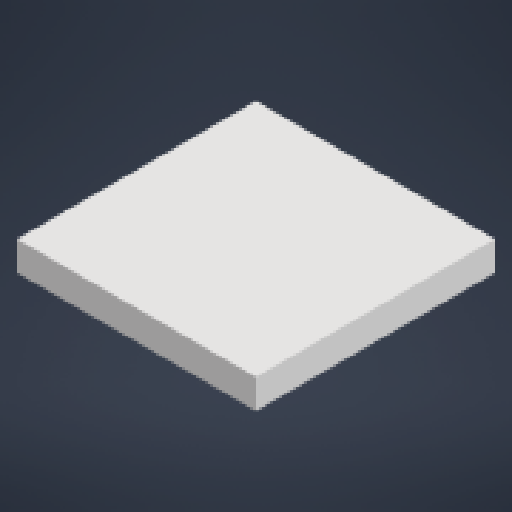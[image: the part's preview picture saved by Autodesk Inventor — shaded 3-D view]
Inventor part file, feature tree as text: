
AUTODESK INVENTOR PART (.ipt)
format: ipt  version: 2023 (Build 270158000, 158)  size: 110,080 bytes
history: native  units: in
note: dims shown in document units (in); Inventor stores cm internally (conversion verified against a paired STEP export)
features: extrude x1, sketch x1
ambient origin geometry x8: Origin, YZ Plane, XZ Plane, XY Plane, X Axis, Y Axis, Z Axis, Center Point
bodies: Solid1 (feature_tree)
feature tree (2):
  extrude  "Extrusion1"  Depth=1.5748in
  sketch  "Sketch1"  dims[d0=1.1811in d1=1.5748in d2=0.1929in d3=0.0in]
